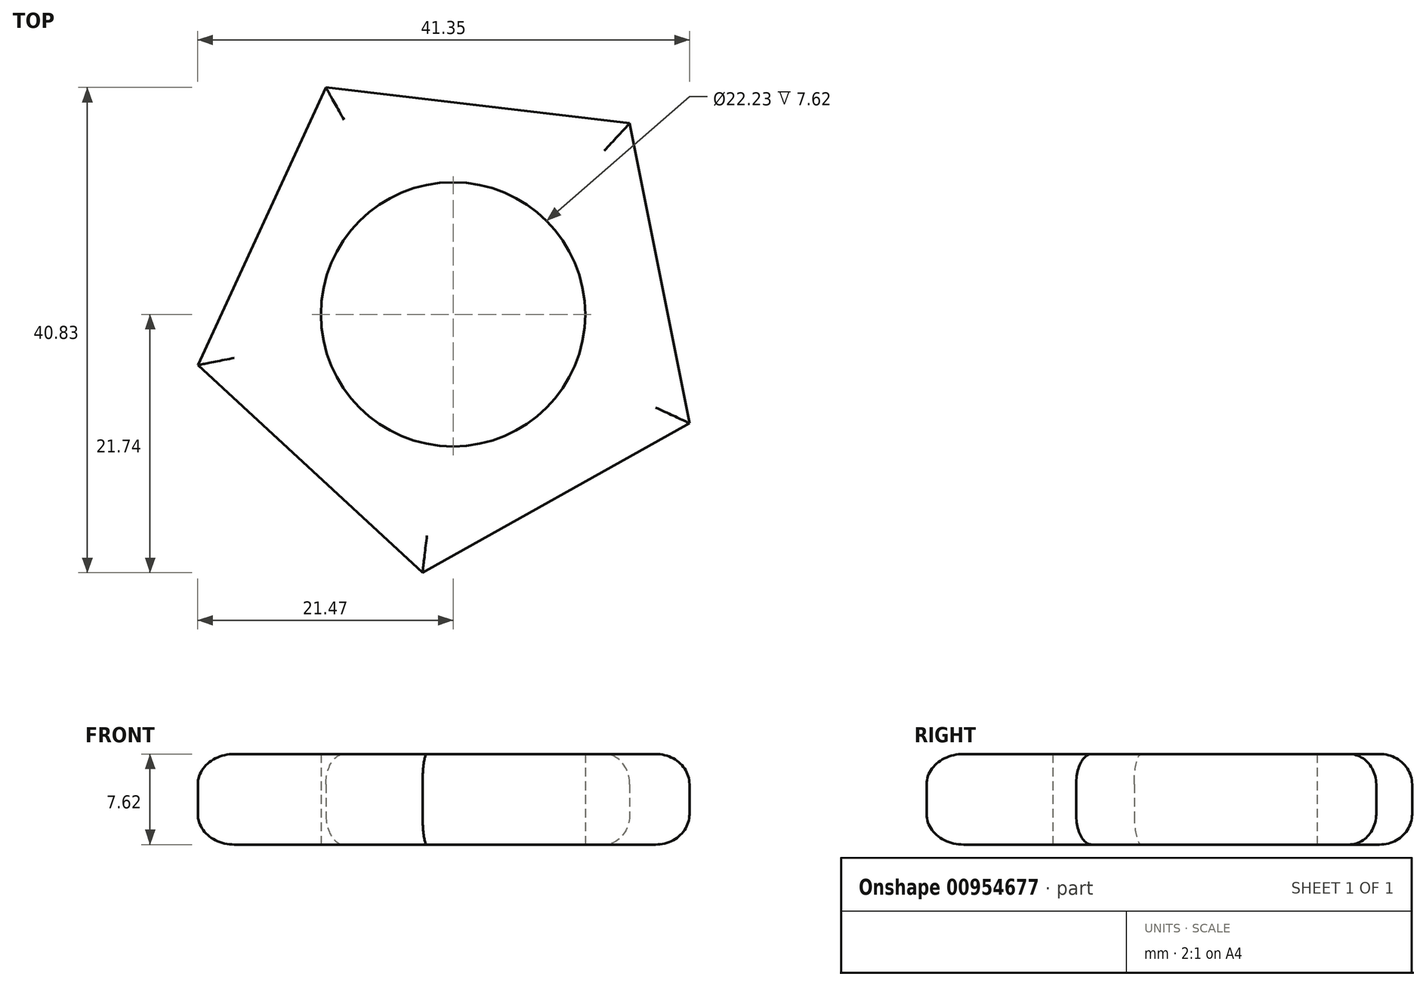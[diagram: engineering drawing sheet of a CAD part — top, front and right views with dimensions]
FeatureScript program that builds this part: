
annotation { "Feature Type Name" : "Feature", "Feature Type Description" : "" }
export const myFeature = defineFeature(function(context is Context, id is Id, definition is map)
    precondition{}
    {
        {
            var Q0;
            Q0=qCreatedBy(makeId("Top.planeOp"),FACE);
            var sketch = newSketch(context, id + "F0", { "sketchPlane" : qUnion([Q0])});
            skCircle(sketch, "E0", {"center": v(0, 0) * mm, "radius": 11.11 * mm});
            skCircle(sketch, "E1.cCircle", {"center": v(0, 0) * mm, "radius": 17.7 * mm, "construction": true});
            skLineSegment(sketch, "E1.0", {"start": v(19.88, -9.16) * mm, "end": v(-2.57, -21.74) * mm});
            skLineSegment(sketch, "E1.1", {"start": v(-2.57, -21.74) * mm, "end": v(-21.47, -4.28) * mm});
            skLineSegment(sketch, "E1.2", {"start": v(-21.47, -4.28) * mm, "end": v(-10.7, 19.1) * mm});
            skLineSegment(sketch, "E1.3", {"start": v(-10.7, 19.1) * mm, "end": v(14.85, 16.08) * mm});
            skLineSegment(sketch, "E1.4", {"start": v(14.85, 16.08) * mm, "end": v(19.88, -9.16) * mm});
            skPoint(sketch, "E1.0.midPoint", {"position": v(8.66, -15.45) * mm});
            skSolve(sketch);
        }
        {
            var Q0;
            Q0=makeQuery(id+"F0.imprint","IMPRINT",FACE,{"disambiguationData":[TD([[makeQuery(id+"F0.imprint","IMPRINT",EDGE,{"derivedFrom":sQuery(id+"F0.wireOp",EDGE,"E0")}),-1.0]])]});
            extrude(context, id + "F1", {"entities" : qUnion([Q0]), "depth" : 7.62 * mm, "offsetDistance" : 25.4 * mm});
        }
        {
            var Q0;
            Q0=makeQuery(id+"F1.opExtrude","CAP_EDGE",EDGE,{"disambiguationData":[OSD([sQuery(id+"F0.wireOp",EDGE,"E1.1")])],"isStart":false});
            var Q1;
            Q1=makeQuery(id+"F1.opExtrude","CAP_EDGE",EDGE,{"disambiguationData":[OSD([sQuery(id+"F0.wireOp",EDGE,"E1.0")])],"isStart":false});
            var Q2;
            Q2=makeQuery(id+"F1.opExtrude","CAP_EDGE",EDGE,{"disambiguationData":[OSD([sQuery(id+"F0.wireOp",EDGE,"E1.4")])],"isStart":false});
            var Q3;
            Q3=makeQuery(id+"F1.opExtrude","CAP_EDGE",EDGE,{"disambiguationData":[OSD([sQuery(id+"F0.wireOp",EDGE,"E1.3")])],"isStart":false});
            var Q4;
            Q4=makeQuery(id+"F1.opExtrude","CAP_EDGE",EDGE,{"disambiguationData":[OSD([sQuery(id+"F0.wireOp",EDGE,"E1.2")])],"isStart":false});
            var Q5;
            Q5=makeQuery(id+"F1.opExtrude","CAP_EDGE",EDGE,{"disambiguationData":[OSD([sQuery(id+"F0.wireOp",EDGE,"E1.0")])],"isStart":true});
            var Q6;
            Q6=makeQuery(id+"F1.opExtrude","CAP_EDGE",EDGE,{"disambiguationData":[OSD([sQuery(id+"F0.wireOp",EDGE,"E1.1")])],"isStart":true});
            var Q7;
            Q7=makeQuery(id+"F1.opExtrude","CAP_EDGE",EDGE,{"disambiguationData":[OSD([sQuery(id+"F0.wireOp",EDGE,"E1.2")])],"isStart":true});
            var Q8;
            Q8=makeQuery(id+"F1.opExtrude","CAP_EDGE",EDGE,{"disambiguationData":[OSD([sQuery(id+"F0.wireOp",EDGE,"E1.3")])],"isStart":true});
            var Q9;
            Q9=makeQuery(id+"F1.opExtrude","CAP_EDGE",EDGE,{"disambiguationData":[OSD([sQuery(id+"F0.wireOp",EDGE,"E1.4")])],"isStart":true});
            fillet(context, id + "F2", {"entities" : qUnion([Q0, Q1, Q2, Q3, Q4, Q5, Q6, Q7, Q8, Q9]), "radius" : 2.54 * mm, "tangentPropagation" : true, "allowEdgeOverflow" : false});
        }
    });
